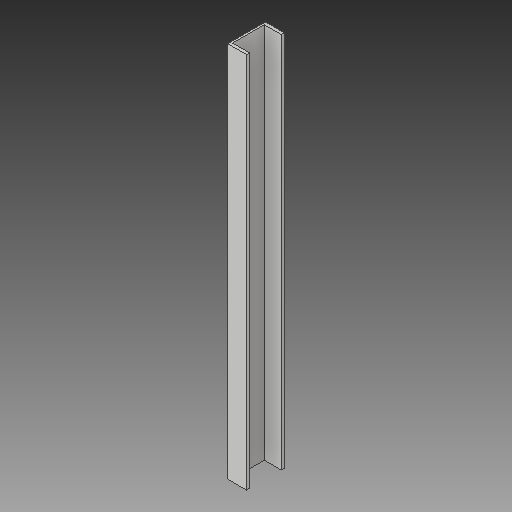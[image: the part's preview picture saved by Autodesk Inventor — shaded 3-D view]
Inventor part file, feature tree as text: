
AUTODESK INVENTOR PART (.ipt)
format: ipt  version: 2019 (Build 230136000, 136)  size: 87,040 bytes
history: native  units: in
note: dims shown in document units (in); Inventor stores cm internally (conversion verified against a paired STEP export)
features: other x3, sketch x1
ambient origin geometry x8: Origin, YZ Plane, XZ Plane, XY Plane, X Axis, Y Axis, Z Axis, Center Point
bodies: Solid1 (feature_tree)
feature tree (4):
  other  "Channel1.ipt"
  other  "Solid1::Channel1.ipt"
  other  "TaggingFeature1"
  sketch  "Sketch1"  dims[d0=0.3937in]
